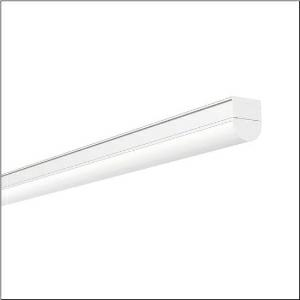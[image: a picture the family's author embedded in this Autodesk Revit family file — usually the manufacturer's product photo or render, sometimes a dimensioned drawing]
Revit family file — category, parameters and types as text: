
# Revit family: ecopack_r__31_51lj12mkm40a_d749
name_source: partatom
category: Lighting Fixtures
units: mm (PartAtom-declared; Revit-internal decimal feet)

## family parameters
Cut with Voids When Loaded = No
Host = Face
Light Source = No
Part Type = Normal
Room Calculation Point = No
Round Connector Dimension = Use Diameter
Shared = No

## types (1)
- --- (1 x LED, 4890 lm, 35 W, 5000K)
    Apparent Load = 35 VA
    CIE Flux Codes = 39 67 87 89 100
    Color Rendering = 80
    Color Temperature = 5000K
    Default Elevation = 1800 mm
    Description = Ecopack® 31, diffuser luminaire, primary optical cover: cover, of PC, frosted, light emission: direct distribution, primary light characteristic: symmetric, installation type: surface-mounted, LED, rated luminous flux: 4.800lm, luminous efficacy: 135lm/W, light colour: 830/840/850, colour temperature: 3000/4000/5000K, control gear: ON/OFF Multilumen, with terminal, 3-pole, mains connection: 220..240V, AC, 50/60Hz, rated input power: 35W, housing, of aluminium, traffic white (RAL 9016), length: 1.150mm, width: 56mm, height: 68mm, end cap, of PC, white, protection rating (complete): IP20, insulation class (complete): insulation class I (protective earthing), certification: CE, impact resistance: IK06, permissible operating ambient temperature: -20..+40°C, packaging unit: 1 piece
    Height = 68 mm
    Lamp = 1 x LED
    Lamp Light Flux = 4890 lm
    Lamp Power = 35 W
    Lamp count = 1
    Length = 1149 mm
    Luminous efficacy = 140 lm/W
    Manufacturer = Siteco
    ModVariant = No
    Model = 51LJ12MKM40A
    Mounting Place = Ceiling
    Mounting Type = Surface mounted
    Number of Poles = 1
    OnlyDefault = Yes
    Power Factor = 1
    Product Name = Ecopack® 31
    Product group = diffuser luminaire
    ProductGroupID = 307
    Protection Class = Protection class I
    Protection Degree = IP 20
    RLX_Detail_Level = 1
    RLX_Emergency_Light_Flux = 0 lm
    RLX_Emergency_Type = 0
    RLX_Emergency_Type_DB = No
    RlxData = <blob elided: 28721 chars, md5=b63b281d>
    Socket = socket
    Standby Power = 0 W
    System Light Flux = 4890 lm
    System Power = 35 W
    Type Comments = individual setting: colour temperature 5000K, luminous flux: 100 % | (ON | ON)
    Type Image = l_1007030.jpg
    URL = http://relux.com
    VarID = @adj_195503
    Voltage = 0 V
    Weight = 0.00 kg
    Width = 56 mm

## geometry (parser evidence)
native form markers: Blend x4, Sweep x12
no freeform markers — native parametric forms only
